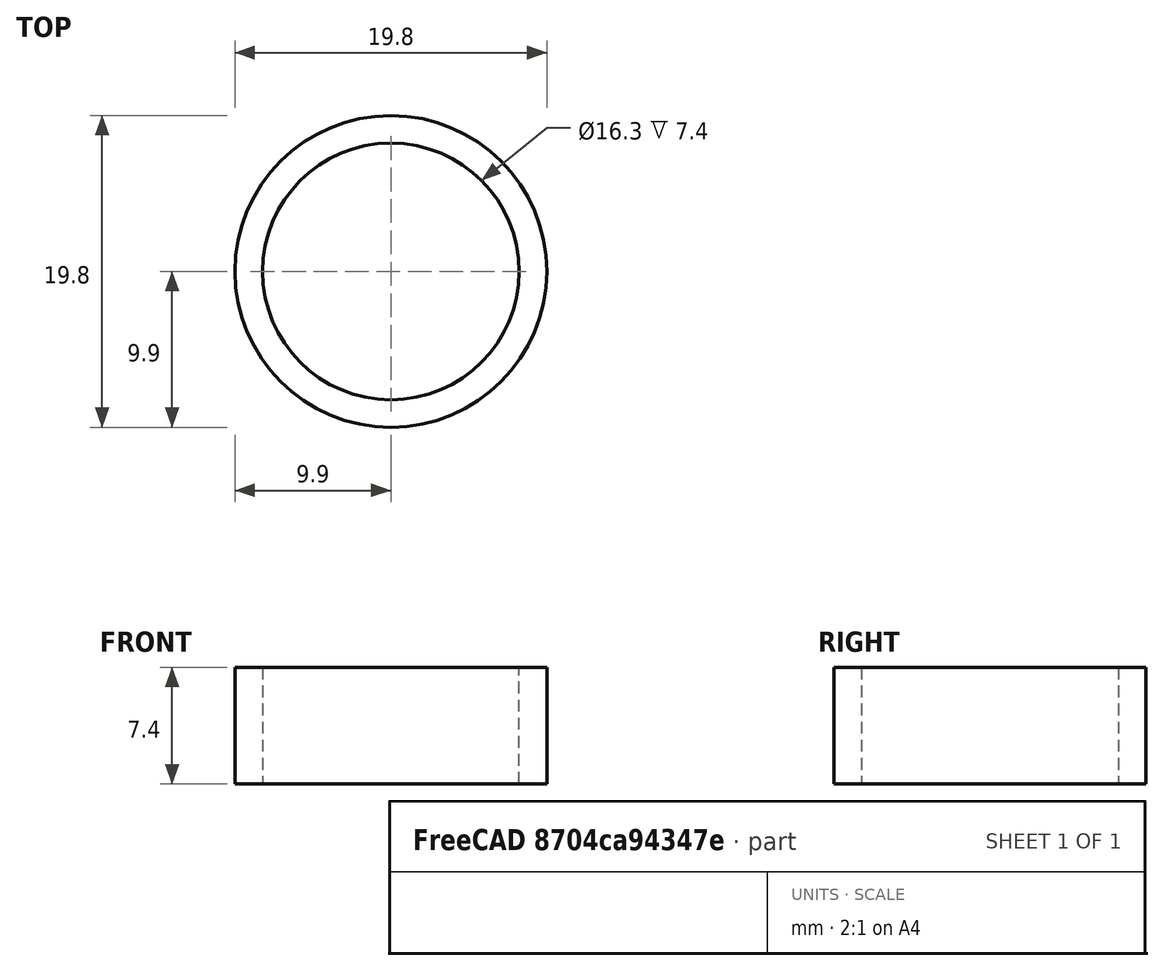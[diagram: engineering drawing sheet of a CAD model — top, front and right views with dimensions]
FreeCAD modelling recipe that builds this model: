
FCSTD DOCUMENT  (FreeCAD 0.20R27319 (Git))
Label: StopORingSleeve
License: All rights reserved
LicenseURL: http://en.wikipedia.org/wiki/All_rights_reserved
objects: Sketcher::SketchObject×1, PartDesign::Pad×1, PartDesign::Body×1
note: 4 computed .brp shape members not serialized (recipe doc carries the construction recipe); baked Part::Feature solids carry a one-line shape summary decoded from their .brp
EXTERNAL_REF file=SharedDimensions.FCStd obj=Spreadsheet

FEATURE [Sketcher::SketchObject] Sketch
  FullyConstrained = true
  MapMode = 5
  Support = -> [XY_Plane]
  expr: Constraints[1] = SharedDimensions#Spreadsheet.HoleDiameter - 2 * SharedDimensions#Spreadsheet.HoleClearance
  expr: Constraints[3] = SharedDimensions#Spreadsheet.HoleDiameter - 2 * SharedDimensions#Spreadsheet.ORingThickness + 0.3
  sketch-geometry (2):
    g0: Circle CenterX=0 CenterY=0 CenterZ=0 NormalX=0 NormalY=0 NormalZ=1 AngleXU=0 Radius=9.9
    g1: Circle CenterX=0 CenterY=0 CenterZ=0 NormalX=0 NormalY=0 NormalZ=1 AngleXU=0 Radius=8.15
  constraints (4):
    c: Coincident(g0,g-1)
    c: Diameter(g0) = 19.8
    c: Coincident(g1,g0)
    c: Diameter(g1) = 16.3
FEATURE [PartDesign::Pad] Pad
  Direction = (0,0,1)
  Length = 7.4
  Length2 = 10
  Profile = -> Sketch
  ReferenceAxis = -> Sketch [N_Axis]
  Type = 0
  expr: Length = 3 * SharedDimensions#Spreadsheet.BenchThickness / 5 - 4
FEATURE [PartDesign::Body] Body
  Group = -> [Sketch,Pad]
  Origin = -> Origin
  Tip = -> Pad
